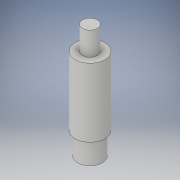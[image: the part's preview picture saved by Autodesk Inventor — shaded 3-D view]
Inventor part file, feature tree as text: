
AUTODESK INVENTOR PART (.ipt)
format: ipt  version: 2019 (Build 230136000, 136)  size: 110,080 bytes
history: native  units: in
note: dims shown in document units (in); Inventor stores cm internally (conversion verified against a paired STEP export)
features: extrude x3, sketch x3, projected_geometry x1
ambient origin geometry x8: Origin, YZ Plane, XZ Plane, XY Plane, X Axis, Y Axis, Z Axis, Center Point
bodies: Solid1 (feature_tree)
feature tree (7):
  extrude  "Extrusion1"  Depth=7.874in TaperAngle=0.0deg
  extrude  "Extrusion2"  Depth=1.6142in TaperAngle=0.0deg
  extrude  "Extrusion3"  [1 undecoded]
  sketch  "Sketch1"  dims[d0=2.0472in d1=7.874in d2=0.0in]
  sketch  "Sketch2"  dims[d3=1.0236in d4=1.6142in d5=0.0in]
  projected_geometry  "Projected Loop1"
  sketch  "Sketch3"  dims[d6=1.5354in d7=0.0in]
note: 1 required parameter value undecoded (feature->parameter linkage not recoverable at this tier; creation-order binding heuristic only, values carry confidence <= 0.55)
